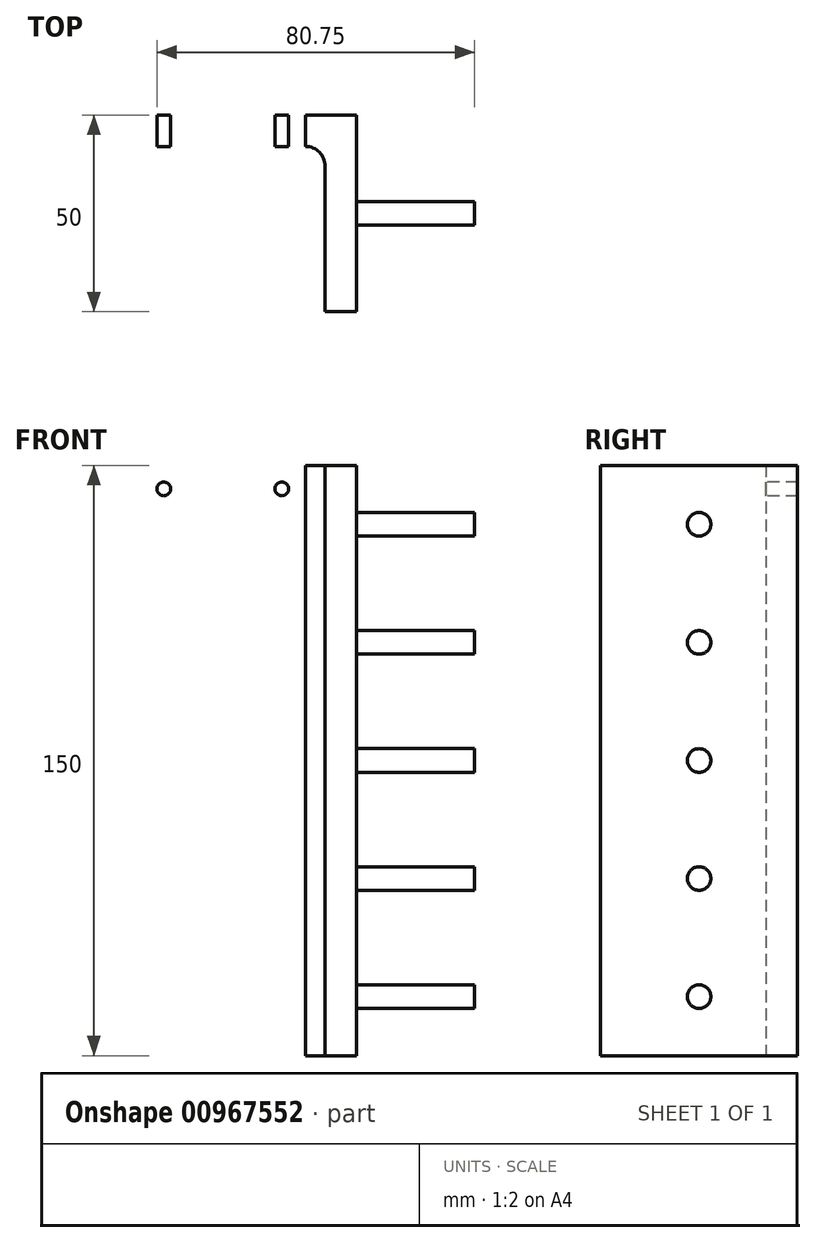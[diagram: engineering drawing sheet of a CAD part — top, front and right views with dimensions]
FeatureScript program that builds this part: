
annotation { "Feature Type Name" : "Feature", "Feature Type Description" : "" }
export const myFeature = defineFeature(function(context is Context, id is Id, definition is map)
    precondition{}
    {
        {
            var Q0;
            Q0=qCreatedBy(makeId("Top.planeOp"),FACE);
            var sketch = newSketch(context, id + "F0", { "sketchPlane" : qUnion([Q0])});
            skLineSegment(sketch, "E0", {"start": v(-49.5, 35.35) * mm, "end": v(-7.5, 35.35) * mm});
            skLineSegment(sketch, "E1", {"start": v(-2.5, 30.35) * mm, "end": v(-2.5, -6.65) * mm});
            skLineSegment(sketch, "E2", {"start": v(-2.5, -6.65) * mm, "end": v(5.5, -6.65) * mm});
            skLineSegment(sketch, "E3", {"start": v(5.5, -6.65) * mm, "end": v(5.5, 43.35) * mm});
            skLineSegment(sketch, "E4", {"start": v(5.5, 43.35) * mm, "end": v(-49.5, 43.35) * mm});
            skLineSegment(sketch, "E5", {"start": v(-49.5, 43.35) * mm, "end": v(-49.5, 35.35) * mm});
            skPoint(sketch, "E6.visualSharp", {"position": v(-2.5, 35.35) * mm});
            skArc(sketch, "E6.filletArc", {"start": v(-2.5, 30.35) * mm, "mid": v(-3.97, 33.89) * mm, "end": v(-7.5, 35.35) * mm});
            skSolve(sketch);
        }
        {
            var Q0;
            Q0=makeQuery(id+"F0.imprint","IMPRINT",FACE,{"disambiguationData":[TD([[makeQuery(id+"F0.imprint","IMPRINT",EDGE,{"derivedFrom":sQuery(id+"F0.wireOp",EDGE,"E0")}),1.0]])]});
            extrude(context, id + "F1", {"entities" : qUnion([Q0]), "depth" : 150 * mm, "offsetDistance" : 25 * mm});
        }
        {
            var Q0;
            Q0=makeQuery(id+"F1.opExtrude","SWEPT_FACE",FACE,{"disambiguationData":[OSD([sQuery(id+"F0.wireOp",EDGE,"E3")])]});
            var sketch = newSketch(context, id + "F2", { "sketchPlane" : qUnion([Q0])});
            skLineSegment(sketch, "E7", {"start": v(18.35, 150) * mm, "end": v(18.35, 0) * mm, "construction": true});
            skCircle(sketch, "E8", {"center": v(18.35, 135) * mm, "radius": 3 * mm});
            skCircle(sketch, "E9", {"center": v(18.35, 105) * mm, "radius": 3 * mm});
            skCircle(sketch, "E10", {"center": v(18.35, 45) * mm, "radius": 3 * mm});
            skCircle(sketch, "E11", {"center": v(18.35, 75) * mm, "radius": 3 * mm});
            skCircle(sketch, "E12", {"center": v(18.35, 15) * mm, "radius": 3 * mm});
            skSolve(sketch);
        }
        {
            var Q0;
            Q0=makeQuery(id+"F2.imprint","IMPRINT",FACE,{"disambiguationData":[TD([[makeQuery(id+"F2.imprint","IMPRINT",EDGE,{"derivedFrom":sQuery(id+"F2.wireOp",EDGE,"E8")}),1.0]])]});
            var Q1;
            Q1=makeQuery(id+"F2.imprint","IMPRINT",FACE,{"disambiguationData":[TD([[makeQuery(id+"F2.imprint","IMPRINT",EDGE,{"derivedFrom":sQuery(id+"F2.wireOp",EDGE,"E9")}),1.0]])]});
            var Q2;
            Q2=makeQuery(id+"F2.imprint","IMPRINT",FACE,{"disambiguationData":[TD([[makeQuery(id+"F2.imprint","IMPRINT",EDGE,{"derivedFrom":sQuery(id+"F2.wireOp",EDGE,"E11")}),1.0]])]});
            var Q3;
            Q3=makeQuery(id+"F2.imprint","IMPRINT",FACE,{"disambiguationData":[TD([[makeQuery(id+"F2.imprint","IMPRINT",EDGE,{"derivedFrom":sQuery(id+"F2.wireOp",EDGE,"E10")}),1.0]])]});
            var Q4;
            Q4=makeQuery(id+"F2.imprint","IMPRINT",FACE,{"disambiguationData":[TD([[makeQuery(id+"F2.imprint","IMPRINT",EDGE,{"derivedFrom":sQuery(id+"F2.wireOp",EDGE,"E12")}),1.0]])]});
            extrude(context, id + "F3", {"entities" : qUnion([Q0, Q1, Q2, Q3, Q4]), "operationType" : NewBodyOperationType.ADD, "depth" : 30 * mm, "offsetDistance" : 25 * mm});
        }
        {
            var Q0;
            Q0=makeQuery(id+"F1.opExtrude","SWEPT_FACE",FACE,{"disambiguationData":[OSD([sQuery(id+"F0.wireOp",EDGE,"E0")])]});
            var sketch = newSketch(context, id + "F4", { "sketchPlane" : qUnion([Q0])});
            skLineSegment(sketch, "E13", {"start": v(-49.5, 75) * mm, "end": v(-7.5, 75) * mm, "construction": true});
            skCircle(sketch, "E14", {"center": v(-43.5, 6) * mm, "radius": 1.75 * mm});
            skCircle(sketch, "E15", {"center": v(-13.5, 6) * mm, "radius": 1.75 * mm});
            skCircle(sketch, "E16.MirrorC", {"center": v(-43.5, 144) * mm, "radius": 1.75 * mm});
            skCircle(sketch, "E17.MirrorC", {"center": v(-13.5, 144) * mm, "radius": 1.75 * mm});
            skSolve(sketch);
        }
        {
            var Q0;
            Q0=makeQuery(id+"F4.imprint","IMPRINT",FACE,{"disambiguationData":[TD([[makeQuery(id+"F4.imprint","IMPRINT",EDGE,{"derivedFrom":sQuery(id+"F4.wireOp",EDGE,"E14")}),1.0]])]});
            var Q1;
            Q1=makeQuery(id+"F4.imprint","IMPRINT",FACE,{"disambiguationData":[TD([[makeQuery(id+"F4.imprint","IMPRINT",EDGE,{"derivedFrom":sQuery(id+"F4.wireOp",EDGE,"E15")}),1.0]])]});
            var Q2;
            Q2=makeQuery(id+"F4.imprint","IMPRINT",FACE,{"disambiguationData":[TD([[makeQuery(id+"F4.imprint","IMPRINT",EDGE,{"derivedFrom":sQuery(id+"F4.wireOp",EDGE,"E16.MirrorC")}),-1.0]])]});
            var Q3;
            Q3=makeQuery(id+"F4.imprint","IMPRINT",FACE,{"disambiguationData":[TD([[makeQuery(id+"F4.imprint","IMPRINT",EDGE,{"derivedFrom":sQuery(id+"F4.wireOp",EDGE,"E17.MirrorC")}),-1.0]])]});
            extrude(context, id + "F5", {"entities" : qUnion([Q0, Q1, Q2, Q3]), "operationType" : NewBodyOperationType.REMOVE, "oppositeDirection" : true, "depth" : 8 * mm, "offsetDistance" : 25 * mm});
        }
    });
